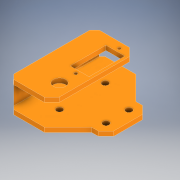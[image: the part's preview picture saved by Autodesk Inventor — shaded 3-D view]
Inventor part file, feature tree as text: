
AUTODESK INVENTOR PART (.ipt)
format: ipt  version: 2021 (Build 250183000, 183)  size: 298,496 bytes
history: native  units: mm
features: extrude x3, sketch x3, projected_geometry x1
ambient origin geometry x8: Origin, YZ Plane, XZ Plane, XY Plane, X Axis, Y Axis, Z Axis, Center Point
bodies: Solid1 (feature_tree)
feature tree (7):
  extrude  "Extrusion1"  Depth=3.0mm TaperAngle=0.0deg
  extrude  "Extrusion7"  Depth=30.0mm
  extrude  "Extrusion8"  Depth=4.0mm
  sketch  "Sketch1"  dims[d0=57.0mm d1=70.0mm d2=3.0mm d3=0.0mm]
  projected_geometry  "Projected Loop1"
  sketch  "Sketch10"  dims[d7=30.0mm d8=30.0mm]
  sketch  "Sketch11"  dims[d12=4.0mm d13=4.0mm d17=4.0mm d18=4.0mm d19=15.0mm d21=7.0mm d22=32.3mm d23=12.4mm d24=4.4mm d25=4.4mm d27=6.2mm d28=11.05mm d36=27.5mm d38=25.0mm d40=25.0mm d47=0.0mm d49=32.2mm d50=32.2mm d52=30.0mm d53=4.9mm d54=2.2mm d57=2.0mm d58=2.0mm d59=1.9mm d60=1.9mm d87=19.7mm d90=15.0mm d91=20.0mm d92=15.0mm d93=20.0mm d111=4.5mm d112=4.5mm d124=70.0mm d132=7.0mm d133=5.0mm d134=5.0mm d135=5.0mm d136=5.0mm d137=5.0mm d138=5.0mm d139=45.0deg d140=15.5mm d141=7.0mm d142=5.0mm d143=5.0mm d144=5.0mm d145=5.0mm d146=25.0mm d147=3.0mm d148=15.1mm d149=0.0mm d150=25.0mm d151=56.077455mm d152=5.0mm d153=5.0mm d154=5.0mm d155=5.0mm d156=8.0mm d157=3.0mm d158=0.0mm d165=15.0mm]
